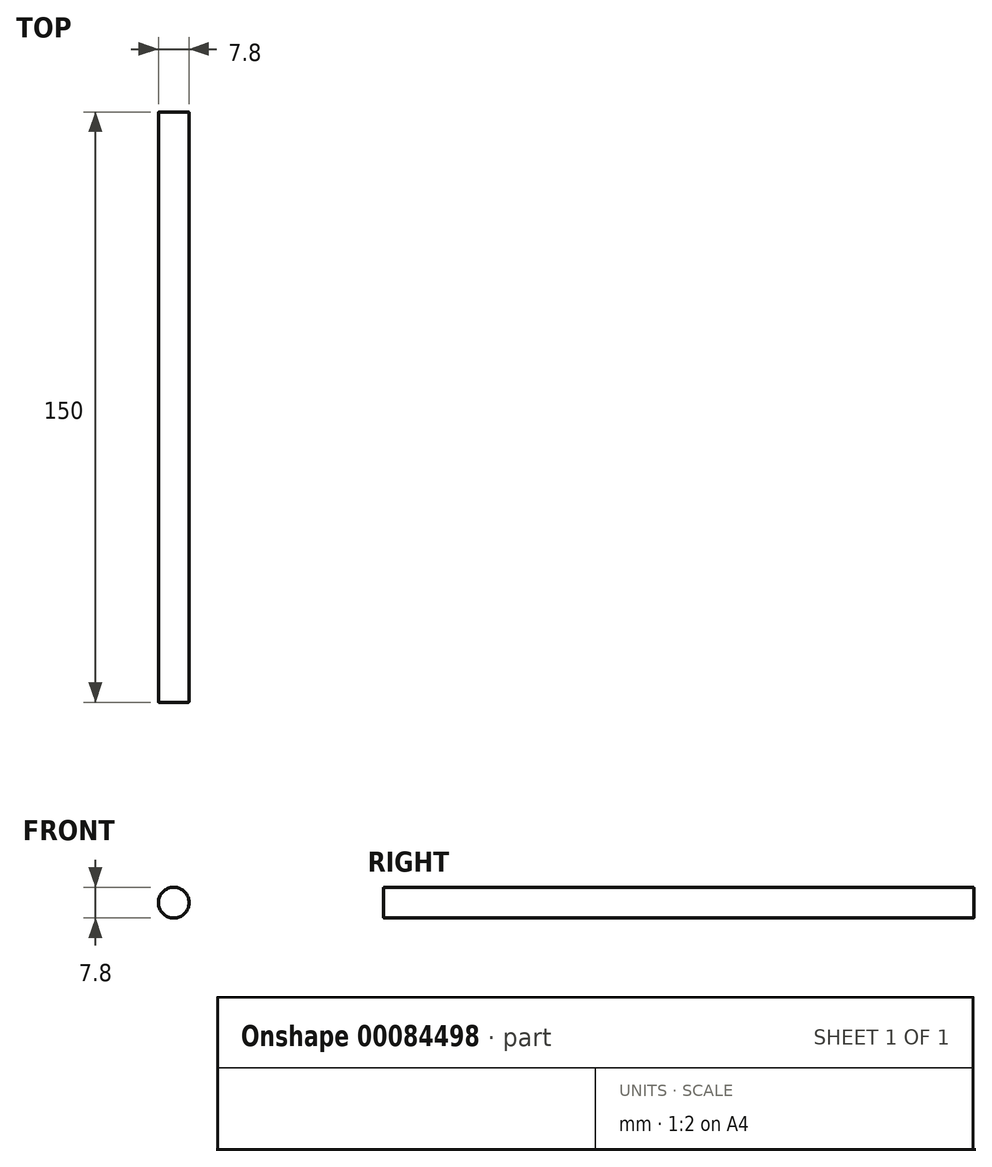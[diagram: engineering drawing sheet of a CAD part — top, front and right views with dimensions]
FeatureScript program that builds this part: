
annotation { "Feature Type Name" : "Feature", "Feature Type Description" : "" }
export const myFeature = defineFeature(function(context is Context, id is Id, definition is map)
    precondition{}
    {
        {
            var Q0;
            Q0=qCreatedBy(makeId("Front.planeOp"),FACE);
            var sketch = newSketch(context, id + "F0", { "sketchPlane" : qUnion([Q0])});
            skCircle(sketch, "E0", {"center": v(0, 0) * mm, "radius": 3.9 * mm});
            skSolve(sketch);
        }
        {
            var Q0;
            Q0=makeQuery(id+"F0.imprint","IMPRINT",FACE,{"disambiguationData":[TD([[makeQuery(id+"F0.imprint","IMPRINT",EDGE,{"derivedFrom":sQuery(id+"F0.wireOp",EDGE,"E0")}),1.0]])]});
            extrude(context, id + "F1", {"entities" : qUnion([Q0]), "endBound" : BoundingType.SYMMETRIC, "depth" : 150 * mm});
        }
        {
            var Q0;
            Q0=makeQuery(id+"F1.opExtrude","CAP_EDGE",EDGE,{"disambiguationData":[OSD([sQuery(id+"F0.wireOp",EDGE,"E0")])],"isStart":false});
            var Q1;
            Q1=makeQuery(id+"F1.opExtrude","CAP_EDGE",EDGE,{"disambiguationData":[OSD([sQuery(id+"F0.wireOp",EDGE,"E0")])],"isStart":true});
            fillet(context, id + "F2", {"entities" : qUnion([Q0, Q1]), "radius" : .2 * mm, "tangentPropagation" : true, "allowEdgeOverflow" : false});
        }
    });
